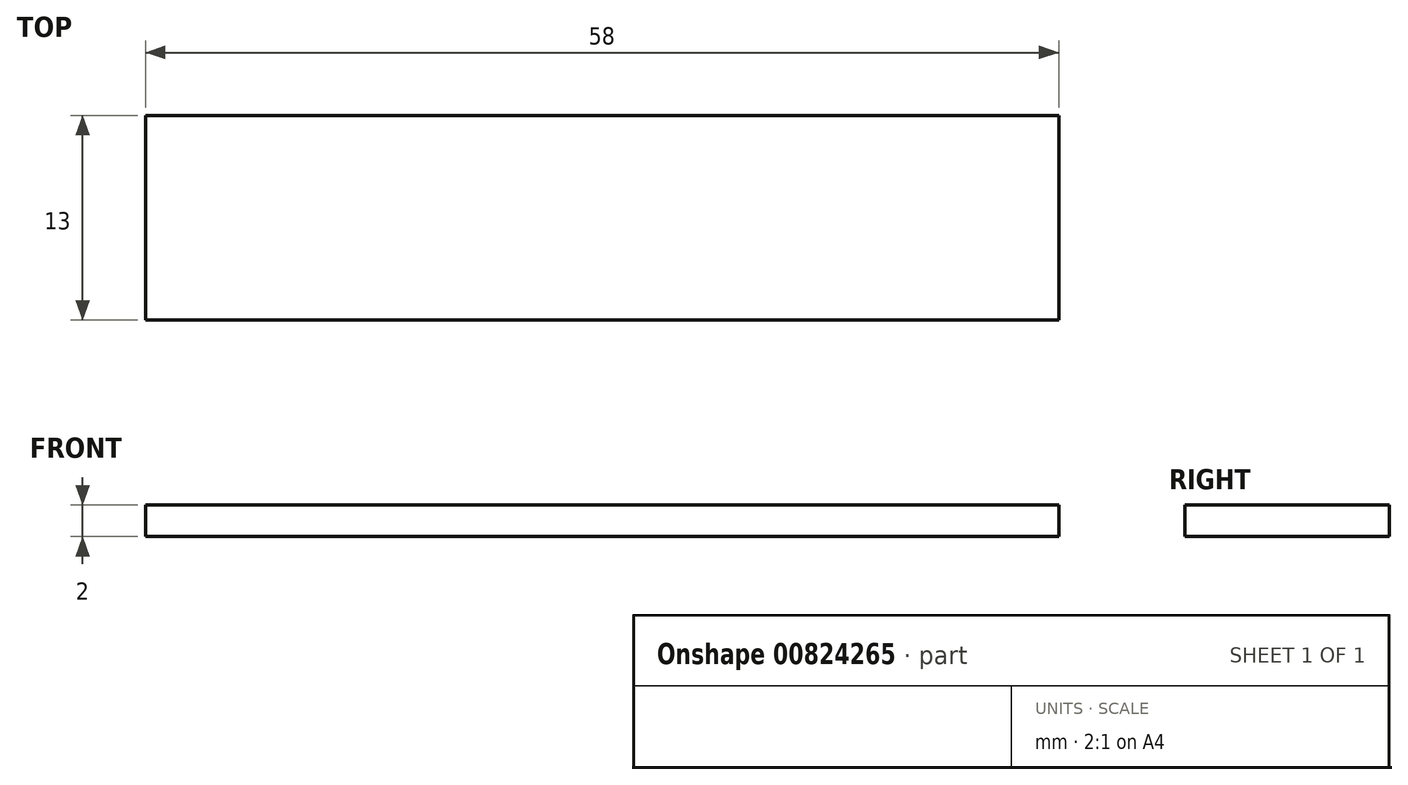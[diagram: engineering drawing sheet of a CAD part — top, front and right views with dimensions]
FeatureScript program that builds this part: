
annotation { "Feature Type Name" : "Feature", "Feature Type Description" : "" }
export const myFeature = defineFeature(function(context is Context, id is Id, definition is map)
    precondition{}
    {
        {
            var Q0;
            Q0=qCreatedBy(makeId("Top.planeOp"),FACE);
            var sketch = newSketch(context, id + "F0", { "sketchPlane" : qUnion([Q0])});
            skLineSegment(sketch, "E0.bottom", {"start": v(29, 6.5) * mm, "end": v(-29, 6.5) * mm});
            skLineSegment(sketch, "E0.top", {"start": v(29, -6.5) * mm, "end": v(-29, -6.5) * mm});
            skLineSegment(sketch, "E0.left", {"start": v(29, 6.5) * mm, "end": v(29, -6.5) * mm});
            skLineSegment(sketch, "E0.right", {"start": v(-29, 6.5) * mm, "end": v(-29, -6.5) * mm});
            skPoint(sketch, "E0.middle", {"position": v(0, 0) * mm});
            skSolve(sketch);
        }
        {
            var Q0;
            Q0=qSketchRegion(id+"F0",true);
            extrude(context, id + "F1", {"entities" : qUnion([Q0]), "depth" : 2 * mm, "offsetDistance" : 25 * mm});
        }
    });
